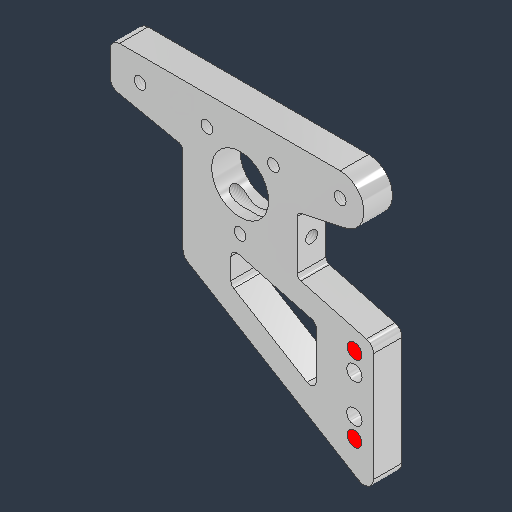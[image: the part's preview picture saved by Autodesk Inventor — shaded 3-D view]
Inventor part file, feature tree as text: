
AUTODESK INVENTOR PART (.ipt)
format: ipt  version: 2024.3 (Build 283343000, 343)  size: 265,216 bytes
history: native  units: in
note: dims shown in document units (in); Inventor stores cm internally (conversion verified against a paired STEP export)
features: sketch x7, hole x6, extrude x2, fillet x2, projected_geometry x1
ambient origin geometry x8: Origin, YZ Plane, XZ Plane, XY Plane, X Axis, Y Axis, Z Axis, Center Point
bodies: Body1 (feature_tree)
feature tree (18):
  extrude  "Extrusion2"  Depth=0.3125in
  hole  "Hole1"  [1 undecoded]
  hole  "Hole2"  [1 undecoded]
  extrude  "Extrusion3"  Depth=0.375in TaperAngle=0.0deg
  hole  "Hole3"  [1 undecoded]
  sketch  "Sketch8"  dims[d44=1.0in d45=0.0625in]
  hole  "Hole5"  [1 undecoded]
  hole  "Hole6"  [1 undecoded]
  fillet  "Fillet4"  Radius=0.5in
  fillet  "Fillet5"  Radius=0.75in
  hole  "Hole9"  [1 undecoded]
  sketch  "Sketch1"  dims[d24=2.005in d25=0.3125in]
  sketch  "Sketch2"  dims[d26=0.75in d27=0.75in]
  sketch  "Sketch3"  dims[d28=105.0deg d30=0.25in]
  sketch  "Sketch4"  dims[d31=1.75in d32=0.375in d33=0.0in]
  sketch  "Sketch6"  dims[d34=0.156in d35=0.38in d36=0.375in d37=0.25in d38=0.5635in d39=1.0in d40=0.8108in d43=0.875in]
  projected_geometry  "Projected Loop1"
  sketch  "Sketch11"  dims[d46=0.156in d47=0.38in d48=0.375in d49=0.19in d50=0.5635in d51=0.536in d52=0.8108in d54=0.75in d55=0.5in d56=0.75in d57=1.125in d58=0.3125in d59=0.3125in d60=0.08in d61=0.0in d62=0.0in d63=0.0625in d64=0.125in d65=0.156in d66=0.38in d67=0.375in d68=0.25in d69=0.5635in d70=1.0in d71=0.8108in d72=1.125in d85=0.5in d86=1.0in d88=0.1875in d89=0.25in d90=0.197in d91=0.75in d92=0.375in d93=0.25in d94=0.5635in d95=1.0in d96=0.8108in d97=0.201in d98=0.38in d99=0.375in d100=0.25in d101=0.5635in d102=1.0in d103=0.8108in d110=1.25in d127=0.395in d128=0.156in d129=0.25in d130=0.375in d131=0.25in d132=0.5635in d133=0.25in d134=0.8108in]
note: 6 required parameter values undecoded (feature->parameter linkage not recoverable at this tier; creation-order binding heuristic only, values carry confidence <= 0.55)
